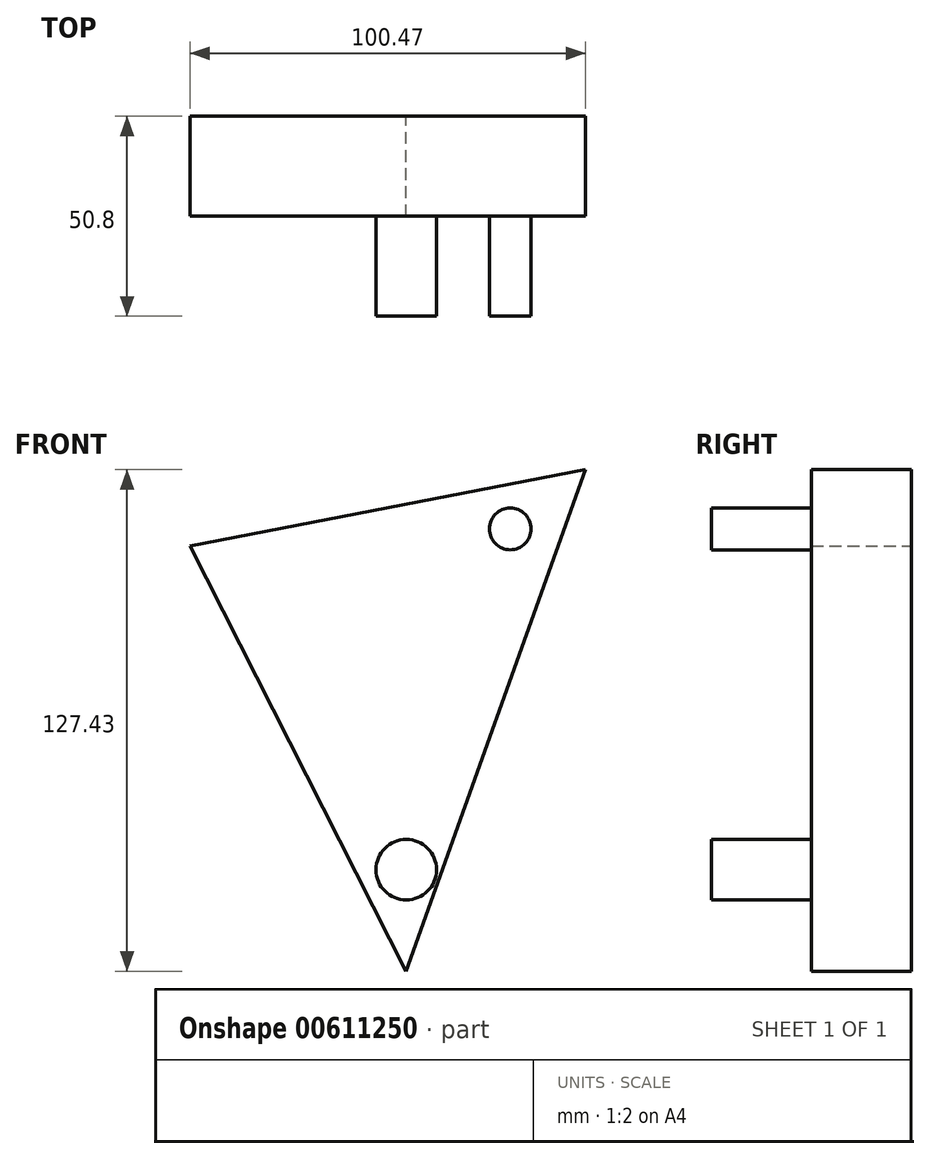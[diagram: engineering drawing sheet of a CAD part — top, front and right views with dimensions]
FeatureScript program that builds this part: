
annotation { "Feature Type Name" : "Feature", "Feature Type Description" : "" }
export const myFeature = defineFeature(function(context is Context, id is Id, definition is map)
    precondition{}
    {
        {
            var Q0;
            Q0=qCreatedBy(makeId("Front.planeOp"),FACE);
            var sketch = newSketch(context, id + "F0", { "sketchPlane" : qUnion([Q0])});
            skLineSegment(sketch, "E0", {"start": v(0, 0) * mm, "end": v(-54.93, 108.02) * mm});
            skLineSegment(sketch, "E1", {"start": v(-54.93, 108.02) * mm, "end": v(45.54, 127.43) * mm});
            skLineSegment(sketch, "E2", {"start": v(45.54, 127.43) * mm, "end": v(0, 0) * mm});
            skSolve(sketch);
        }
        {
            var Q0;
            Q0=makeQuery(id+"F0.imprint","IMPRINT",FACE,{"disambiguationData":[TD([[makeQuery(id+"F0.imprint","IMPRINT",EDGE,{"derivedFrom":sQuery(id+"F0.wireOp",EDGE,"E0")}),-1.0]])]});
            extrude(context, id + "F1", {"entities" : qUnion([Q0]), "depth" : 50.8 * mm, "offsetDistance" : 25.4 * mm});
        }
        {
            var Q0;
            Q0=makeQuery(id+"F1.opExtrude","CAP_FACE",FACE,{"disambiguationData":[OSD([sQuery(id+"F0.wireOp",EDGE,"E0"),sQuery(id+"F0.wireOp",EDGE,"E1"),sQuery(id+"F0.wireOp",EDGE,"E2")])],"isStart":false});
            var sketch = newSketch(context, id + "F2", { "sketchPlane" : qUnion([Q0])});
            skCircle(sketch, "E3", {"center": v(26.41, 112.38) * mm, "radius": 5.3 * mm});
            skSolve(sketch);
        }
        {
            var Q0;
            Q0=makeQuery(id+"F2.imprint","IMPRINT",FACE,{"disambiguationData":[TD([[makeQuery(id+"F2.imprint","IMPRINT",EDGE,{"derivedFrom":sQuery(id+"F2.wireOp",EDGE,"E3")}),-1.0]])]});
            var sketch = newSketch(context, id + "F3", { "sketchPlane" : qUnion([Q0])});
            skCircle(sketch, "E4", {"center": v(0, 25.8) * mm, "radius": 7.7 * mm});
            skSolve(sketch);
        }
        {
            var Q0;
            Q0=makeQuery(id+"F3.imprint","IMPRINT",FACE,{"disambiguationData":[TD([[makeQuery(id+"F3.imprint","IMPRINT",EDGE,{"derivedFrom":sQuery(id+"F3.wireOp",EDGE,"E4")}),-1.0]])]});
            var Q1;
            Q1=sQuery(id+"F2.wireOp",EDGE,"E3");
            extrude(context, id + "F4", {"entities" : qUnion([Q0]), "operationType" : NewBodyOperationType.REMOVE, "surfaceEntities" : qUnion([Q1]), "oppositeDirection" : true, "depth" : 25.4 * mm, "offsetDistance" : 25.4 * mm});
        }
    });
